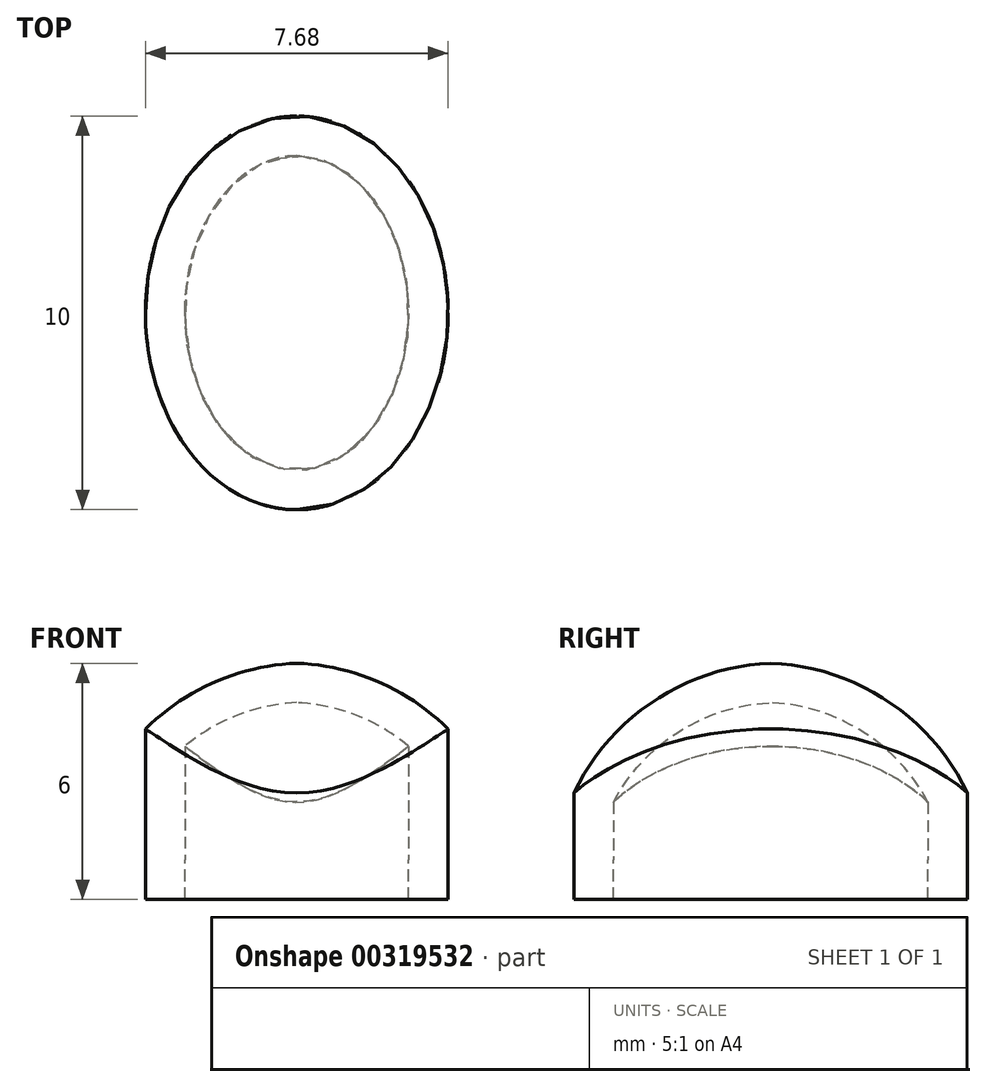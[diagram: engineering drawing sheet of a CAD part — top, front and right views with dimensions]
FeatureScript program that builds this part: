
annotation { "Feature Type Name" : "Feature", "Feature Type Description" : "" }
export const myFeature = defineFeature(function(context is Context, id is Id, definition is map)
    precondition{}
    {
        {
            var Q0;
            Q0=qCreatedBy(makeId("Top.planeOp"),FACE);
            var sketch = newSketch(context, id + "F0", { "sketchPlane" : qUnion([Q0])});
            skEllipse(sketch, "E0", {"center": v(0, 0) * mm, "majorRadius": 5 * mm, "minorRadius": 3.84 * mm, "majorAxis": v(0, -1)});
            skSolve(sketch);
        }
        {
            var Q0;
            Q0=makeQuery(id+"F0.imprint","IMPRINT",FACE,{"disambiguationData":[TD([[makeQuery(id+"F0.imprint","IMPRINT",EDGE,{"derivedFrom":sQuery(id+"F0.wireOp",EDGE,"E0")}),1.0]])]});
            extrude(context, id + "F1", {"entities" : qUnion([Q0]), "depth" : 5 * mm});
        }
        {
            var Q0;
            Q0=qCreatedBy(makeId("Right.planeOp"),FACE);
            var sketch = newSketch(context, id + "F2", { "sketchPlane" : qUnion([Q0])});
            skLineSegment(sketch, "E1", {"start": v(5, 5) * mm, "end": v(5, 0) * mm});
            skLineSegment(sketch, "E2.0", {"start": v(5, 0) * mm, "end": v(-5, 0) * mm});
            skLineSegment(sketch, "E3", {"start": v(0, 0) * mm, "end": v(0, 5) * mm, "construction": true});
            skArc(sketch, "E4", {"start": v(5, 1.7) * mm, "mid": v(2.96, 4.05) * mm, "end": v(0, 5) * mm});
            skLineSegment(sketch, "E5", {"start": v(0, 5) * mm, "end": v(0, 5.55) * mm});
            skLineSegment(sketch, "E6", {"start": v(0, 5.55) * mm, "end": v(6.01, 5.55) * mm});
            skLineSegment(sketch, "E7", {"start": v(6.01, 5.55) * mm, "end": v(6.01, 1.7) * mm});
            skLineSegment(sketch, "E8", {"start": v(6.01, 1.7) * mm, "end": v(5, 1.7) * mm});
            skSolve(sketch);
        }
        {
            var Q0;
            Q0=makeQuery(id+"F2.imprint","IMPRINT",FACE,{"disambiguationData":[TD([[makeQuery(id+"F2.imprint","IMPRINT",EDGE,{"derivedFrom":sQuery(id+"F2.wireOp",EDGE,"E4")}),-1.0]])]});
            var Q1;
            Q1=sQuery(id+"F2.wireOp",EDGE,"E3");
            revolve(context, id + "F3", {"operationType" : NewBodyOperationType.REMOVE, "entities" : qUnion([Q0]), "axis" : qUnion([Q1]), "revolveType" : RevolveType.FULL, "oppositeDirection" : true});
        }
        {
            var Q0;
            Q0=makeQuery(id+"F1.opExtrude","CAP_FACE",FACE,{"disambiguationData":[OSD([sQuery(id+"F0.wireOp",EDGE,"E0")])],"isStart":true});
            shell(context, id + "F4", {"entities" : qUnion([Q0]), "thickness" : 1 * mm});
        }
        {
            var Q0;
            Q0=makeQuery(id+"F1.opExtrude","CAP_FACE",FACE,{"disambiguationData":[OSD([sQuery(id+"F0.wireOp",EDGE,"E0")])],"isStart":true});
            var sketch = newSketch(context, id + "F5", { "sketchPlane" : qUnion([Q0])});
            skEllipse(sketch, "E9.0", {"center": v(0, 0) * mm, "majorRadius": 5 * mm, "minorRadius": 3.84 * mm, "majorAxis": v(0, 1)});
            skFitSpline(sketch, "E10.0", {"points": [v(0.95, 5.67) * mm, v(0, 5.8) * mm, v(-0.95, 5.67) * mm, v(-1.84, 5.32) * mm, v(-2.65, 4.75) * mm, v(-3.33, 4.02) * mm, v(-3.89, 3.14) * mm, v(-4.3, 2.15) * mm, v(-4.54, 1.1) * mm, v(-4.62, 0) * mm, v(-4.54, -1.1) * mm, v(-4.3, -2.15) * mm, v(-3.89, -3.14) * mm, v(-3.33, -4.02) * mm, v(-2.65, -4.75) * mm, v(-1.84, -5.32) * mm, v(-0.95, -5.67) * mm, v(0, -5.8) * mm, v(0.95, -5.67) * mm, v(1.84, -5.32) * mm, v(2.65, -4.75) * mm, v(3.33, -4.02) * mm, v(3.89, -3.14) * mm, v(4.3, -2.15) * mm, v(4.54, -1.1) * mm, v(4.62, 0) * mm, v(4.54, 1.1) * mm, v(4.3, 2.15) * mm, v(3.89, 3.14) * mm, v(3.33, 4.02) * mm, v(2.65, 4.75) * mm, v(1.84, 5.32) * mm, v(0.95, 5.67) * mm, v(0, 5.8) * mm, v(-0.95, 5.67) * mm, v(0.95, 5.67) * mm]});
            skSolve(sketch);
        }
        {
            var Q0;
            Q0=makeQuery(id+"F5.imprint","IMPRINT",FACE,{"disambiguationData":[TD([[makeQuery(id+"F5.imprint","IMPRINT",EDGE,{"derivedFrom":sQuery(id+"F5.wireOp",EDGE,"E9.0")}),1.0]])]});
            var Q1;
            Q1=makeQuery(id+"F5.imprint","IMPRINT",FACE,{"disambiguationData":[TD([[makeQuery(id+"F5.imprint","IMPRINT",EDGE,{"derivedFrom":sQuery(id+"F5.wireOp",EDGE,"E9.0")}),-1.0]])]});
            extrude(context, id + "F6", {"entities" : qUnion([Q0, Q1]), "operationType" : NewBodyOperationType.ADD, "depth" : 1 * mm});
        }
    });
